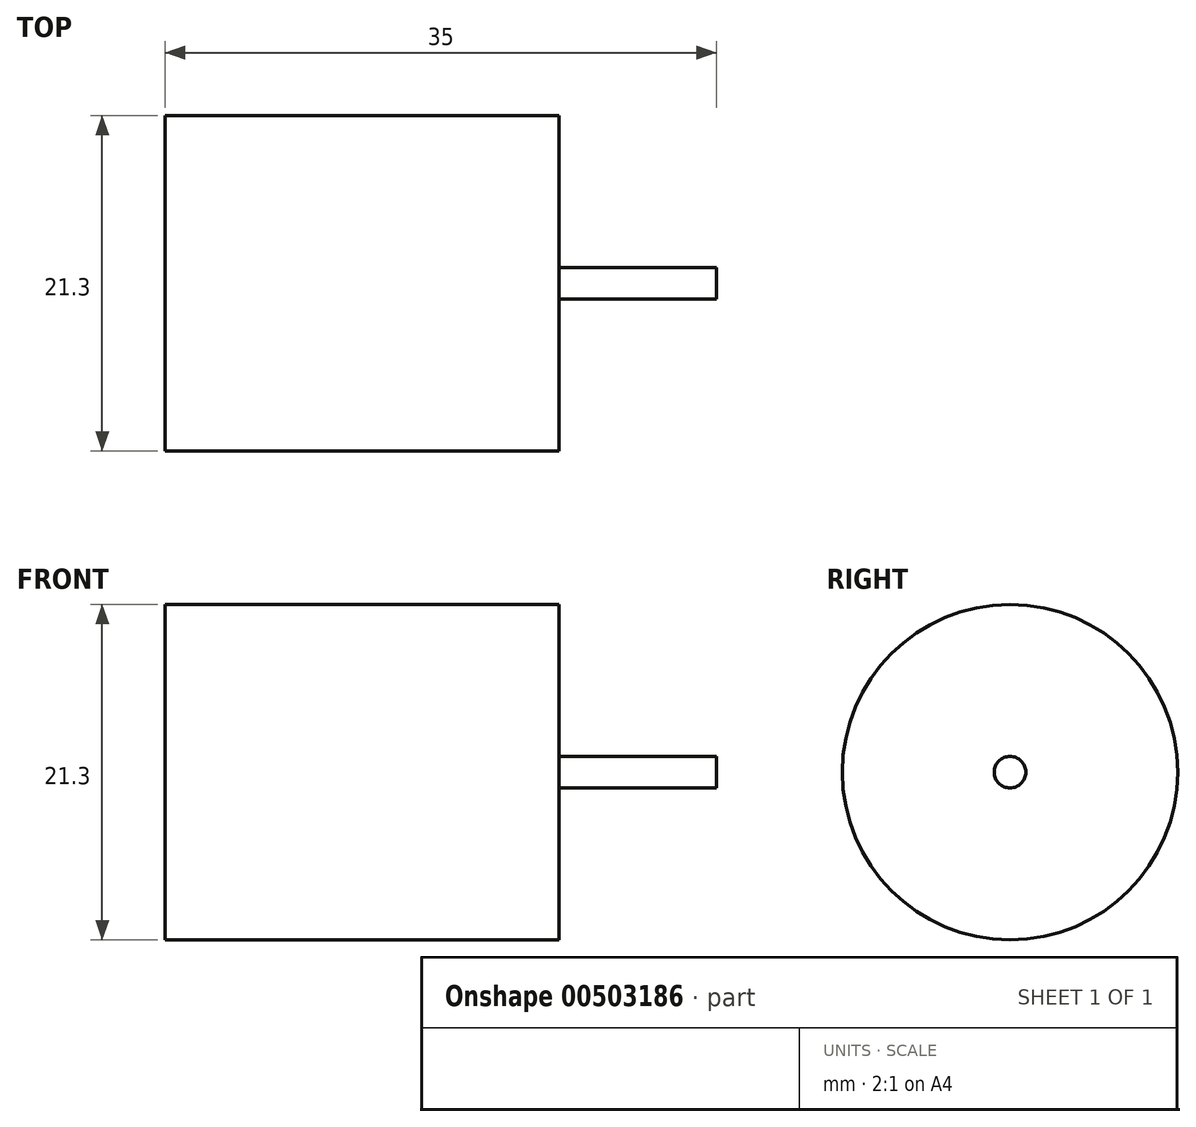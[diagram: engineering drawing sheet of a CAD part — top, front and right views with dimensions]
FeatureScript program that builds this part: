
annotation { "Feature Type Name" : "Feature", "Feature Type Description" : "" }
export const myFeature = defineFeature(function(context is Context, id is Id, definition is map)
    precondition{}
    {
        {
            var Q0;
            Q0=qCreatedBy(makeId("Front.planeOp"),FACE);
            var sketch = newSketch(context, id + "F0", { "sketchPlane" : qUnion([Q0])});
            skLineSegment(sketch, "E0", {"start": v(26.54, 0) * mm, "end": v(26.54, 1) * mm});
            skLineSegment(sketch, "E1", {"start": v(26.54, 1) * mm, "end": v(16.54, 1) * mm});
            skLineSegment(sketch, "E2", {"start": v(16.54, 1) * mm, "end": v(16.54, 10.65) * mm});
            skLineSegment(sketch, "E3", {"start": v(16.54, 10.65) * mm, "end": v(-8.46, 10.65) * mm});
            skLineSegment(sketch, "E4", {"start": v(-8.46, 10.65) * mm, "end": v(-8.46, 0) * mm});
            skLineSegment(sketch, "E5", {"start": v(-8.46, 0) * mm, "end": v(26.54, 0) * mm});
            skSolve(sketch);
        }
        {
            var Q0;
            Q0 = qSketchRegion(id + "F0", true);
            var Q1;
            Q1=sQuery(id+"F0.wireOp",EDGE,"E5");
            revolve(context, id + "F1", {"entities" : qUnion([Q0]), "axis" : qUnion([Q1]), "revolveType" : RevolveType.FULL});
        }
    });
